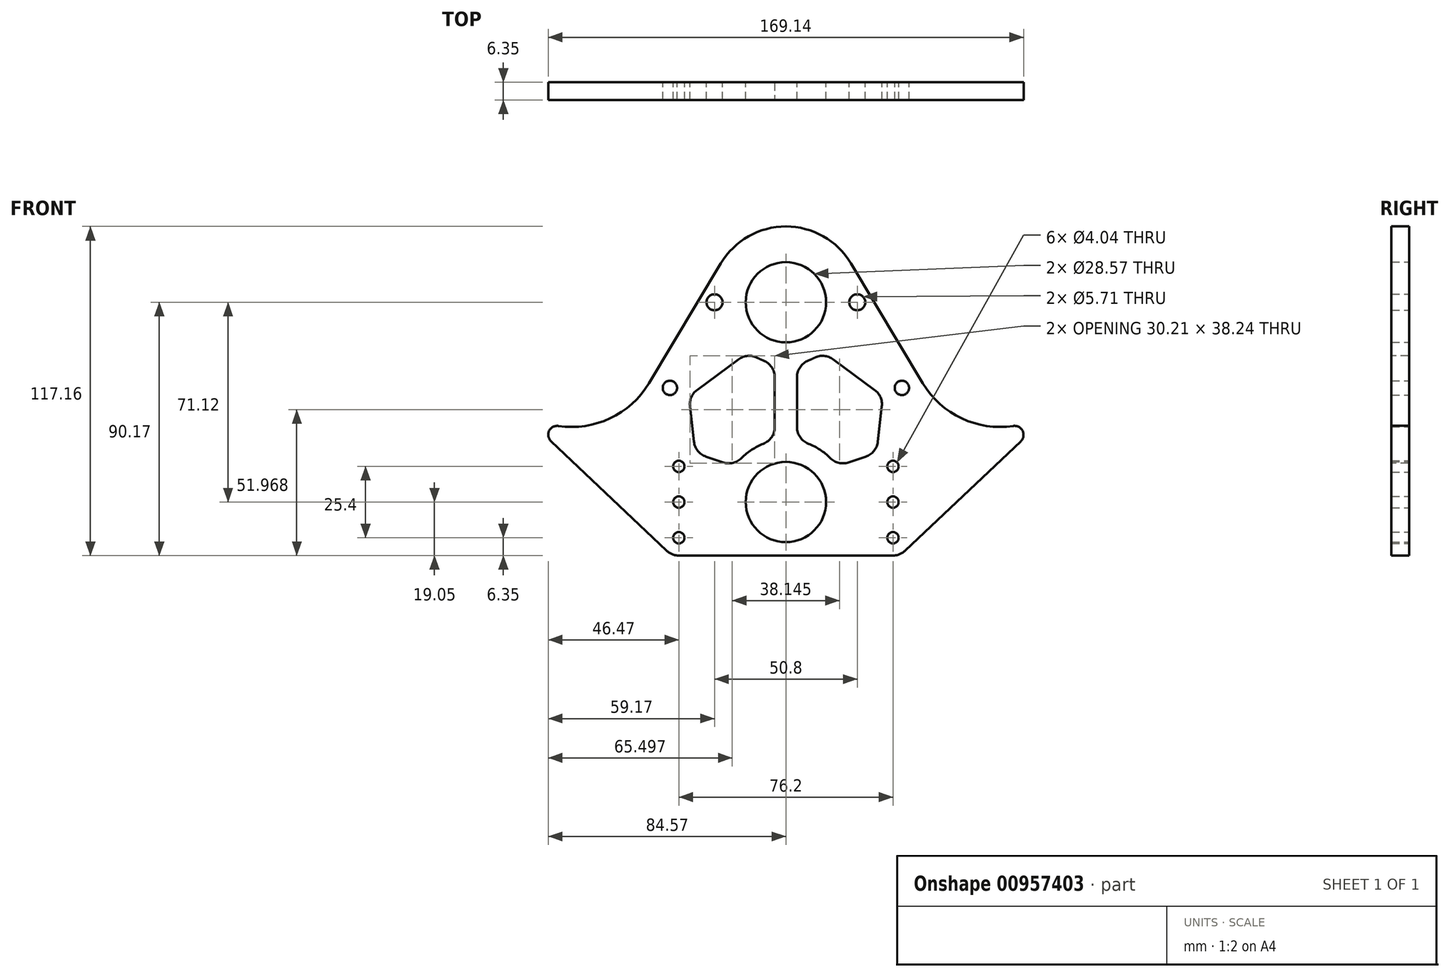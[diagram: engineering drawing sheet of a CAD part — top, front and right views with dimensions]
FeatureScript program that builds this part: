
annotation { "Feature Type Name" : "Feature", "Feature Type Description" : "" }
export const myFeature = defineFeature(function(context is Context, id is Id, definition is map)
    precondition{}
    {
        {
            var Q0;
            Q0=qCreatedBy(makeId("Front.planeOp"),FACE);
            var sketch = newSketch(context, id + "F0", { "sketchPlane" : qUnion([Q0])});
            skCircle(sketch, "E0", {"center": v(-76.2, 58.74) * mm, "radius": 32 * mm, "construction": true});
            skCircle(sketch, "E1", {"center": v(76.2, 58.74) * mm, "radius": 32 * mm, "construction": true});
            skLineSegment(sketch, "E2", {"start": v(-76.2, 58.74) * mm, "end": v(76.2, 58.74) * mm, "construction": true});
            skLineSegment(sketch, "E3", {"start": v(0, 58.74) * mm, "end": v(0, 0) * mm, "construction": true});
            skLineSegment(sketch, "E4.bottom", {"start": v(-127, 23.81) * mm, "end": v(127, 23.81) * mm, "construction": true});
            skLineSegment(sketch, "E4.top", {"start": v(-127, -26.99) * mm, "end": v(127, -26.99) * mm, "construction": true});
            skLineSegment(sketch, "E4.left", {"start": v(-127, 23.81) * mm, "end": v(-127, -26.99) * mm, "construction": true});
            skLineSegment(sketch, "E4.right", {"start": v(127, 23.81) * mm, "end": v(127, -26.99) * mm, "construction": true});
            skPoint(sketch, "E4.middle", {"position": v(0, -1.59) * mm});
            skCircle(sketch, "E5", {"center": v(0, 0) * mm, "radius": 50.8 * mm, "construction": true});
            skCircle(sketch, "E6", {"center": v(0, 71.12) * mm, "radius": 34.3 * mm, "construction": true});
            skCircle(sketch, "E7", {"center": v(0, 71.12) * mm, "radius": 26.99 * mm, "construction": true});
            skCircle(sketch, "E8", {"center": v(0, 71.12) * mm, "radius": 38.1 * mm, "construction": true});
            skCircle(sketch, "E9", {"center": v(0, 0) * mm, "radius": 33.02 * mm, "construction": true});
            skCircle(sketch, "E10", {"center": v(0, 0) * mm, "radius": 44.13 * mm, "construction": true});
            skCircle(sketch, "E11", {"center": v(0, 71.12) * mm, "radius": 14.29 * mm});
            skCircle(sketch, "E12", {"center": v(0, 0) * mm, "radius": 14.29 * mm});
            skCircle(sketch, "E13", {"center": v(-38.1, 12.7) * mm, "radius": 6.35 * mm, "construction": true});
            skCircle(sketch, "E14", {"center": v(-38.1, -12.7) * mm, "radius": 6.35 * mm, "construction": true});
            skCircle(sketch, "E15", {"center": v(38.1, -12.7) * mm, "radius": 6.35 * mm, "construction": true});
            skCircle(sketch, "E16", {"center": v(38.1, 12.7) * mm, "radius": 6.35 * mm, "construction": true});
            skCircle(sketch, "E17", {"center": v(38.1, 0) * mm, "radius": 6.35 * mm, "construction": true});
            skCircle(sketch, "E18", {"center": v(-38.1, 0) * mm, "radius": 6.35 * mm, "construction": true});
            skCircle(sketch, "E19", {"center": v(38.1, -12.7) * mm, "radius": 2.02 * mm});
            skCircle(sketch, "E20", {"center": v(38.1, 0) * mm, "radius": 2.02 * mm});
            skCircle(sketch, "E21", {"center": v(38.1, 12.7) * mm, "radius": 2.02 * mm});
            skCircle(sketch, "E22", {"center": v(-38.1, 12.7) * mm, "radius": 2.02 * mm});
            skCircle(sketch, "E23", {"center": v(-38.1, 0) * mm, "radius": 2.02 * mm});
            skCircle(sketch, "E24", {"center": v(-38.1, -12.7) * mm, "radius": 2.02 * mm});
            skArc(sketch, "E25", {"start": v(-80.92, 27.08) * mm, "mid": v(-62.53, 29.8) * mm, "end": v(-48.75, 42.28) * mm});
            skLineSegment(sketch, "E26", {"start": v(-83.58, 21.64) * mm, "end": v(-42.47, -17.3) * mm});
            skPoint(sketch, "E27.visualSharp", {"position": v(-98.21, 35.5) * mm});
            skArc(sketch, "E27.filletArc", {"start": v(-80.92, 27.08) * mm, "mid": v(-84.25, 25.33) * mm, "end": v(-83.58, 21.64) * mm});
            skLineSegment(sketch, "E28", {"start": v(-48.75, 42.28) * mm, "end": v(-23.15, 85) * mm});
            skArc(sketch, "E29", {"start": v(-23.15, 85) * mm, "mid": v(0, 98.1) * mm, "end": v(23.15, 85) * mm});
            skLineSegment(sketch, "E30", {"start": v(23.15, 85) * mm, "end": v(48.75, 42.28) * mm});
            skArc(sketch, "E31", {"start": v(48.75, 42.28) * mm, "mid": v(62.53, 29.8) * mm, "end": v(80.92, 27.08) * mm});
            skLineSegment(sketch, "E32", {"start": v(83.58, 21.64) * mm, "end": v(42.47, -17.3) * mm});
            skArc(sketch, "E33", {"start": v(-42.47, -17.3) * mm, "mid": v(-40.45, -18.6) * mm, "end": v(-38.1, -19.05) * mm});
            skArc(sketch, "E34", {"start": v(42.47, -17.3) * mm, "mid": v(40.45, -18.6) * mm, "end": v(38.1, -19.05) * mm});
            skLineSegment(sketch, "E35", {"start": v(38.1, -19.05) * mm, "end": v(-38.1, -19.05) * mm});
            skPoint(sketch, "E36.visualSharp", {"position": v(98.21, 35.5) * mm});
            skArc(sketch, "E36.filletArc", {"start": v(83.58, 21.64) * mm, "mid": v(84.25, 25.33) * mm, "end": v(80.92, 27.08) * mm});
            skLineSegment(sketch, "E37.bottom", {"start": v(-38.1, 12.7) * mm, "end": v(38.1, 12.7) * mm, "construction": true});
            skLineSegment(sketch, "E37.top", {"start": v(-38.1, -12.7) * mm, "end": v(38.1, -12.7) * mm, "construction": true});
            skLineSegment(sketch, "E37.left", {"start": v(-38.1, 12.7) * mm, "end": v(-38.1, -12.7) * mm, "construction": true});
            skLineSegment(sketch, "E37.right", {"start": v(38.1, 12.7) * mm, "end": v(38.1, -12.7) * mm, "construction": true});
            skLineSegment(sketch, "E38", {"start": v(-25.4, 71.12) * mm, "end": v(0, 71.12) * mm, "construction": true});
            skLineSegment(sketch, "E39", {"start": v(0, 71.12) * mm, "end": v(25.4, 71.12) * mm, "construction": true});
            skCircle(sketch, "E40", {"center": v(-25.4, 71.12) * mm, "radius": 4.76 * mm, "construction": true});
            skCircle(sketch, "E41", {"center": v(25.4, 71.12) * mm, "radius": 4.76 * mm, "construction": true});
            skCircle(sketch, "E42", {"center": v(-25.4, 71.12) * mm, "radius": 2.86 * mm});
            skCircle(sketch, "E43", {"center": v(25.4, 71.12) * mm, "radius": 2.86 * mm});
            skCircle(sketch, "E44", {"center": v(41.28, 40.64) * mm, "radius": 6.35 * mm, "construction": true});
            skCircle(sketch, "E45", {"center": v(41.28, 40.64) * mm, "radius": 2.55 * mm});
            skCircle(sketch, "E46.MirrorC", {"center": v(-41.28, 40.64) * mm, "radius": 6.35 * mm, "construction": true});
            skCircle(sketch, "E47.MirrorC", {"center": v(-41.28, 40.64) * mm, "radius": 2.55 * mm});
            skSolve(sketch);
        }
        {
            var Q0;
            Q0=qSketchRegion(id+"F0",true);
            extrude(context, id + "F1", {"entities" : qUnion([Q0]), "depth" : 6.35 * mm, "offsetDistance" : 25.4 * mm});
        }
        {
            var Q0;
            Q0=makeQuery(id+"F1.opExtrude","CAP_FACE",FACE,{"disambiguationData":[OSD([sQuery(id+"F0.wireOp",EDGE,"E11"),sQuery(id+"F0.wireOp",EDGE,"E12"),sQuery(id+"F0.wireOp",EDGE,"E19"),sQuery(id+"F0.wireOp",EDGE,"E20"),sQuery(id+"F0.wireOp",EDGE,"E21"),sQuery(id+"F0.wireOp",EDGE,"E22"),sQuery(id+"F0.wireOp",EDGE,"E23"),sQuery(id+"F0.wireOp",EDGE,"E24"),sQuery(id+"F0.wireOp",EDGE,"E25"),sQuery(id+"F0.wireOp",EDGE,"E26"),sQuery(id+"F0.wireOp",EDGE,"E27.filletArc"),sQuery(id+"F0.wireOp",EDGE,"E28"),sQuery(id+"F0.wireOp",EDGE,"E29"),sQuery(id+"F0.wireOp",EDGE,"E30"),sQuery(id+"F0.wireOp",EDGE,"E31"),sQuery(id+"F0.wireOp",EDGE,"E32"),sQuery(id+"F0.wireOp",EDGE,"E33"),sQuery(id+"F0.wireOp",EDGE,"E34"),sQuery(id+"F0.wireOp",EDGE,"E35"),sQuery(id+"F0.wireOp",EDGE,"E36.filletArc"),sQuery(id+"F0.wireOp",EDGE,"E42"),sQuery(id+"F0.wireOp",EDGE,"E43"),sQuery(id+"F0.wireOp",EDGE,"E45"),sQuery(id+"F0.wireOp",EDGE,"E47.MirrorC")])],"isStart":false});
            var sketch = newSketch(context, id + "F2", { "sketchPlane" : qUnion([Q0])});
            skCircle(sketch, "E48", {"center": v(0, 0) * mm, "radius": 22.23 * mm, "construction": true});
            skCircle(sketch, "E49", {"center": v(0, 71.12) * mm, "radius": 22.23 * mm, "construction": true});
            skLineSegment(sketch, "E50", {"start": v(0, 71.12) * mm, "end": v(0, 0) * mm, "construction": true});
            skLineSegment(sketch, "E51", {"start": v(3.97, 21.87) * mm, "end": v(3.97, 49.25) * mm});
            skLineSegment(sketch, "E52", {"start": v(-3.97, 21.87) * mm, "end": v(-3.97, 49.25) * mm});
            skCircle(sketch, "E53", {"center": v(-38.1, 12.7) * mm, "radius": 7.94 * mm, "construction": true});
            skCircle(sketch, "E54", {"center": v(38.1, 12.7) * mm, "radius": 7.94 * mm, "construction": true});
            skCircle(sketch, "E55", {"center": v(41.28, 40.64) * mm, "radius": 7.94 * mm, "construction": true});
            skCircle(sketch, "E56", {"center": v(-41.28, 40.64) * mm, "radius": 7.94 * mm, "construction": true});
            skLineSegment(sketch, "E57", {"start": v(-38.1, 12.7) * mm, "end": v(-41.28, 40.64) * mm, "construction": true});
            skLineSegment(sketch, "E58", {"start": v(-41.28, 40.64) * mm, "end": v(0, 71.12) * mm, "construction": true});
            skLineSegment(sketch, "E59", {"start": v(0, 0) * mm, "end": v(-38.1, 12.7) * mm, "construction": true});
            skLineSegment(sketch, "E60.0", {"start": v(-34.55, 37.71) * mm, "end": v(-13.36, 53.36) * mm});
            skLineSegment(sketch, "E60.1", {"start": v(-32.25, 17.44) * mm, "end": v(-34.55, 37.71) * mm});
            skLineSegment(sketch, "E60.2", {"start": v(-18.2, 12.76) * mm, "end": v(-32.25, 17.44) * mm});
            skArc(sketch, "E61", {"start": v(-3.97, 21.87) * mm, "mid": v(-11.98, 18.72) * mm, "end": v(-18.2, 12.76) * mm});
            skArc(sketch, "E62", {"start": v(-3.97, 49.25) * mm, "mid": v(-8.9, 50.76) * mm, "end": v(-13.36, 53.36) * mm});
            skLineSegment(sketch, "E63.MirrorCS", {"start": v(0, 0) * mm, "end": v(38.1, 12.7) * mm, "construction": true});
            skArc(sketch, "E64.MirrorCS", {"start": v(3.97, 49.25) * mm, "mid": v(8.9, 50.76) * mm, "end": v(13.36, 53.36) * mm});
            skLineSegment(sketch, "E65.MirrorCS", {"start": v(34.55, 37.71) * mm, "end": v(13.36, 53.36) * mm});
            skLineSegment(sketch, "E66.MirrorCS", {"start": v(38.1, 12.7) * mm, "end": v(41.28, 40.64) * mm, "construction": true});
            skLineSegment(sketch, "E67.MirrorCS", {"start": v(18.2, 12.76) * mm, "end": v(32.25, 17.44) * mm});
            skArc(sketch, "E68.MirrorCS", {"start": v(3.97, 21.87) * mm, "mid": v(11.98, 18.72) * mm, "end": v(18.2, 12.76) * mm});
            skLineSegment(sketch, "E69.MirrorCS", {"start": v(41.28, 40.64) * mm, "end": v(0, 71.12) * mm, "construction": true});
            skLineSegment(sketch, "E70.MirrorCS", {"start": v(32.25, 17.44) * mm, "end": v(34.55, 37.71) * mm});
            skSolve(sketch);
        }
        {
            var Q0;
            Q0 = qSketchRegion(id + "F2", true);
            extrude(context, id + "F3", {"entities" : qUnion([Q0]), "operationType" : NewBodyOperationType.REMOVE, "endBound" : BoundingType.THROUGH_ALL, "oppositeDirection" : true, "depth" : 25.4 * mm, "offsetDistance" : 25.4 * mm});
        }
        {
            var Q0;
            Q0=makeQuery(id+"F3.boolean.opBoolean","COPY",EDGE,{"derivedFrom":makeQuery(id+"F3.opExtrude","SWEPT_EDGE",EDGE,{"disambiguationData":[OSD([sQuery(id+"F2.wireOp",EDGE,"E60.0"),sQuery(id+"F2.wireOp",EDGE,"E62")])]})});
            var Q1;
            Q1=makeQuery(id+"F3.boolean.opBoolean","COPY",EDGE,{"derivedFrom":makeQuery(id+"F3.opExtrude","SWEPT_EDGE",EDGE,{"disambiguationData":[OSD([sQuery(id+"F2.wireOp",EDGE,"E62"),sQuery(id+"F2.wireOp",EDGE,"E52")])]})});
            var Q2;
            Q2=makeQuery(id+"F3.boolean.opBoolean","COPY",EDGE,{"derivedFrom":makeQuery(id+"F3.opExtrude","SWEPT_EDGE",EDGE,{"disambiguationData":[OSD([sQuery(id+"F2.wireOp",EDGE,"E61"),sQuery(id+"F2.wireOp",EDGE,"E52")])]})});
            var Q3;
            Q3=makeQuery(id+"F3.boolean.opBoolean","COPY",EDGE,{"derivedFrom":makeQuery(id+"F3.opExtrude","SWEPT_EDGE",EDGE,{"disambiguationData":[OSD([sQuery(id+"F2.wireOp",EDGE,"E60.2"),sQuery(id+"F2.wireOp",EDGE,"E61")])]})});
            var Q4;
            Q4=makeQuery(id+"F3.boolean.opBoolean","COPY",EDGE,{"derivedFrom":makeQuery(id+"F3.opExtrude","SWEPT_EDGE",EDGE,{"disambiguationData":[OSD([sQuery(id+"F2.wireOp",EDGE,"E60.1"),sQuery(id+"F2.wireOp",EDGE,"E60.2")])]})});
            var Q5;
            Q5=makeQuery(id+"F3.boolean.opBoolean","COPY",EDGE,{"derivedFrom":makeQuery(id+"F3.opExtrude","SWEPT_EDGE",EDGE,{"disambiguationData":[OSD([sQuery(id+"F2.wireOp",EDGE,"E60.0"),sQuery(id+"F2.wireOp",EDGE,"E60.1")])]})});
            var Q6;
            Q6=makeQuery(id+"F3.boolean.opBoolean","COPY",EDGE,{"derivedFrom":makeQuery(id+"F3.opExtrude","SWEPT_EDGE",EDGE,{"disambiguationData":[OSD([sQuery(id+"F2.wireOp",EDGE,"E64.MirrorCS"),sQuery(id+"F2.wireOp",EDGE,"E51")])]})});
            var Q7;
            Q7=makeQuery(id+"F3.boolean.opBoolean","COPY",EDGE,{"derivedFrom":makeQuery(id+"F3.opExtrude","SWEPT_EDGE",EDGE,{"disambiguationData":[OSD([sQuery(id+"F2.wireOp",EDGE,"E64.MirrorCS"),sQuery(id+"F2.wireOp",EDGE,"E65.MirrorCS")])]})});
            var Q8;
            Q8=makeQuery(id+"F3.boolean.opBoolean","COPY",EDGE,{"derivedFrom":makeQuery(id+"F3.opExtrude","SWEPT_EDGE",EDGE,{"disambiguationData":[OSD([sQuery(id+"F2.wireOp",EDGE,"E65.MirrorCS"),sQuery(id+"F2.wireOp",EDGE,"E70.MirrorCS")])]})});
            var Q9;
            Q9=makeQuery(id+"F3.boolean.opBoolean","COPY",EDGE,{"derivedFrom":makeQuery(id+"F3.opExtrude","SWEPT_EDGE",EDGE,{"disambiguationData":[OSD([sQuery(id+"F2.wireOp",EDGE,"E67.MirrorCS"),sQuery(id+"F2.wireOp",EDGE,"E70.MirrorCS")])]})});
            var Q10;
            Q10=makeQuery(id+"F3.boolean.opBoolean","COPY",EDGE,{"derivedFrom":makeQuery(id+"F3.opExtrude","SWEPT_EDGE",EDGE,{"disambiguationData":[OSD([sQuery(id+"F2.wireOp",EDGE,"E67.MirrorCS"),sQuery(id+"F2.wireOp",EDGE,"E68.MirrorCS")])]})});
            var Q11;
            Q11=makeQuery(id+"F3.boolean.opBoolean","COPY",EDGE,{"derivedFrom":makeQuery(id+"F3.opExtrude","SWEPT_EDGE",EDGE,{"disambiguationData":[OSD([sQuery(id+"F2.wireOp",EDGE,"E68.MirrorCS"),sQuery(id+"F2.wireOp",EDGE,"E51")])]})});
            fillet(context, id + "F4", {"entities" : qUnion([Q0, Q1, Q2, Q3, Q4, Q5, Q6, Q7, Q8, Q9, Q10, Q11]), "radius" : 6.35 * mm, "tangentPropagation" : true, "allowEdgeOverflow" : false});
        }
    });
